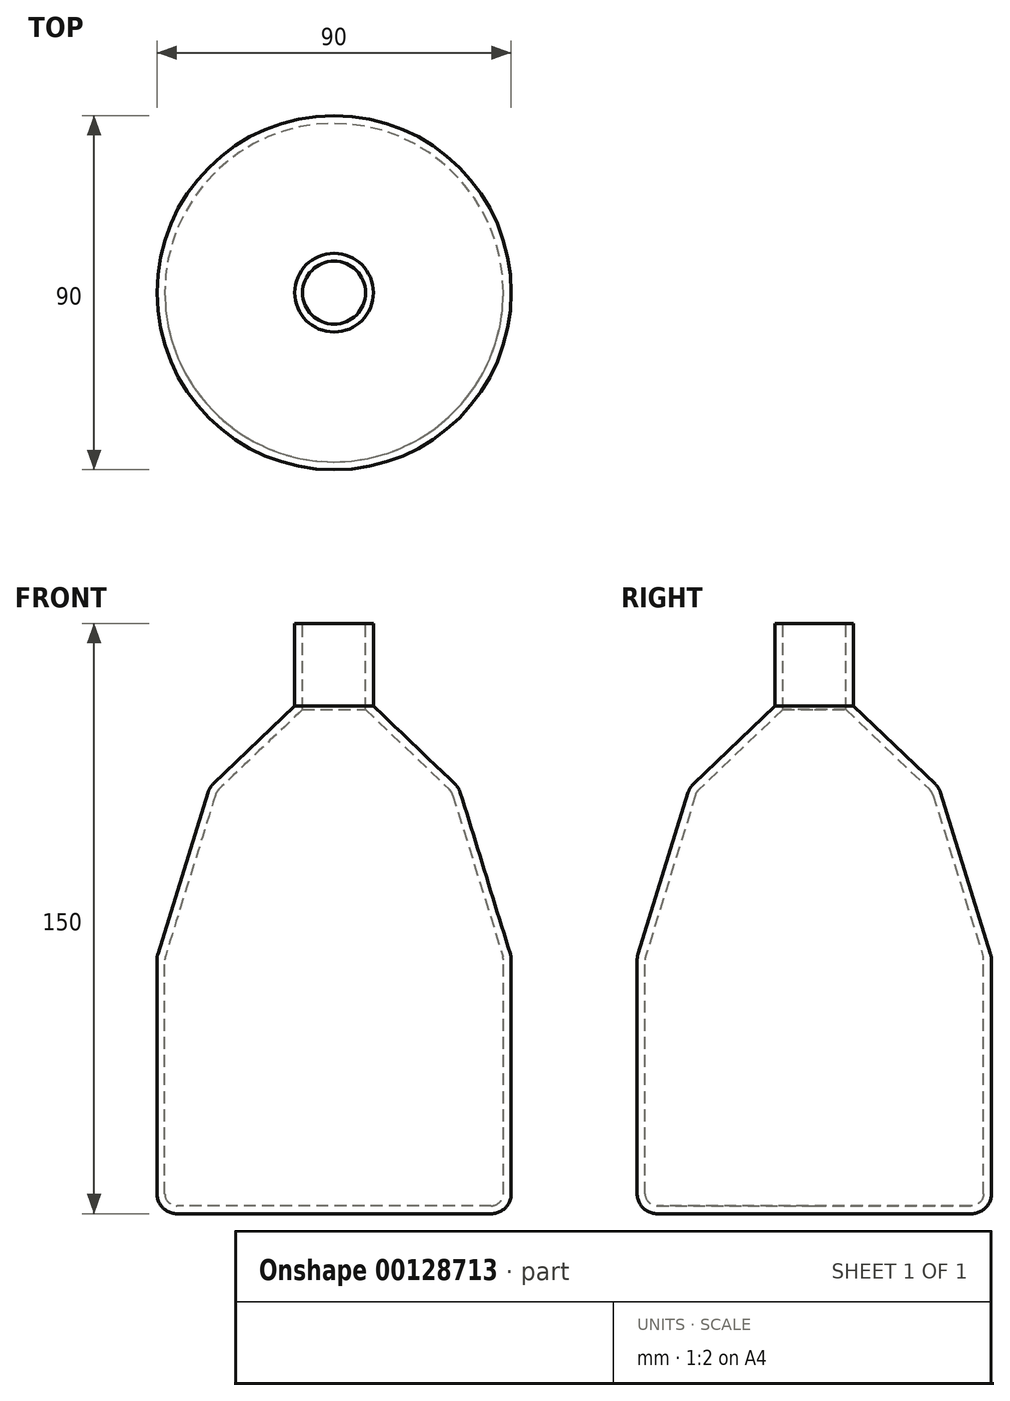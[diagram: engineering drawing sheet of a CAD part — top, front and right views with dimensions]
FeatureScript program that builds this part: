
annotation { "Feature Type Name" : "Feature", "Feature Type Description" : "" }
export const myFeature = defineFeature(function(context is Context, id is Id, definition is map)
    precondition{}
    {
        {
            var Q0;
            Q0=qCreatedBy(makeId("Front.planeOp"),FACE);
            var sketch = newSketch(context, id + "F0", { "sketchPlane" : qUnion([Q0])});
            skLineSegment(sketch, "E0", {"start": v(0, 0) * mm, "end": v(45, 0) * mm});
            skLineSegment(sketch, "E1", {"start": v(45, 0) * mm, "end": v(45, 65.28) * mm});
            skLineSegment(sketch, "E2", {"start": v(45, 65.28) * mm, "end": v(31.66, 108.25) * mm});
            skLineSegment(sketch, "E3", {"start": v(31.66, 108.25) * mm, "end": v(10, 129) * mm});
            skLineSegment(sketch, "E4", {"start": v(10, 129) * mm, "end": v(10, 150) * mm});
            skLineSegment(sketch, "E5", {"start": v(10, 150) * mm, "end": v(0, 150) * mm});
            skLineSegment(sketch, "E6", {"start": v(0, 150) * mm, "end": v(0, 0) * mm});
            skSolve(sketch);
        }
        {
            var Q0;
            Q0=makeQuery(id+"F0.imprint","IMPRINT",FACE,{"disambiguationData":[TD([[makeQuery(id+"F0.imprint","IMPRINT",EDGE,{"derivedFrom":sQuery(id+"F0.wireOp",EDGE,"E0")}),1.0]])]});
            var Q1;
            Q1=sQuery(id+"F0.wireOp",EDGE,"E6");
            revolve(context, id + "F1", {"entities" : qUnion([Q0]), "axis" : qUnion([Q1]), "revolveType" : RevolveType.FULL});
        }
        {
            var Q0;
            Q0=makeQuery(id+"F1.opRevolve","SWEPT_FACE",FACE,{"disambiguationData":[OSD([sQuery(id+"F0.wireOp",EDGE,"E1")])]});
            fillet(context, id + "F2", {"entities" : qUnion([Q0]), "radius" : 5.08 * mm, "tangentPropagation" : true, "allowEdgeOverflow" : false});
        }
        {
            var Q0;
            Q0=makeQuery(id+"F1.opRevolve","SWEPT_EDGE",EDGE,{"disambiguationData":[OSD([sQuery(id+"F0.wireOp",EDGE,"E2"),sQuery(id+"F0.wireOp",EDGE,"E3")])]});
            fillet(context, id + "F3", {"entities" : qUnion([Q0]), "radius" : 5.08 * mm, "tangentPropagation" : true, "allowEdgeOverflow" : false});
        }
        {
            var Q0;
            Q0=makeQuery(id+"F1.opRevolve","SWEPT_FACE",FACE,{"disambiguationData":[OSD([sQuery(id+"F0.wireOp",EDGE,"E5")])]});
            shell(context, id + "F4", {"entities" : qUnion([Q0]), "thickness" : 2 * mm});
        }
    });
